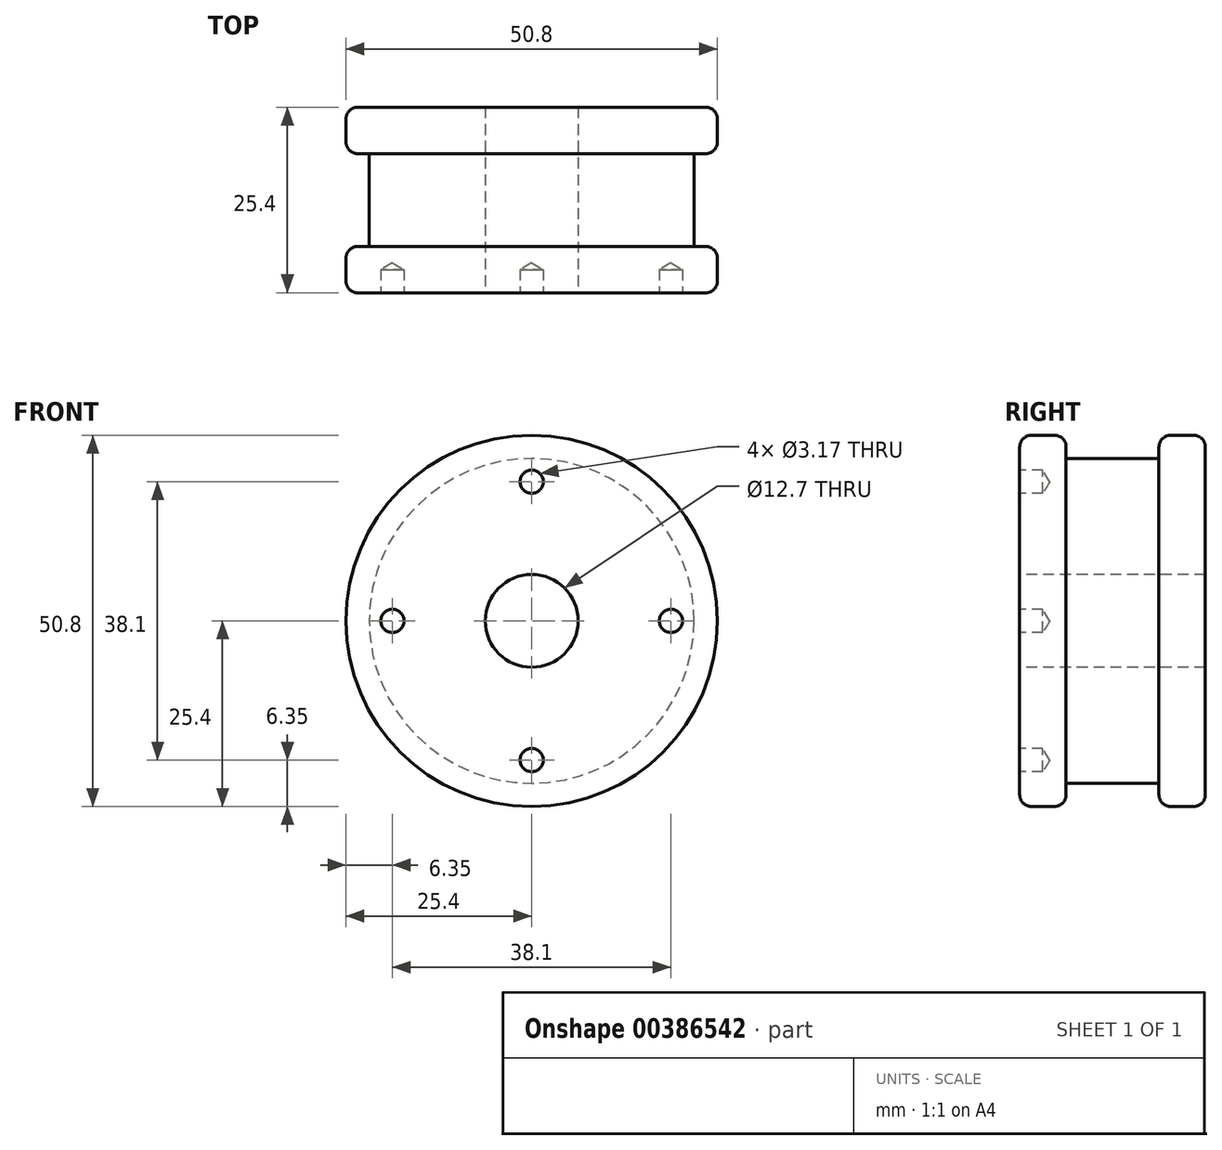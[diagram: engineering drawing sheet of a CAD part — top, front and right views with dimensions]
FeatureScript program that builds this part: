
annotation { "Feature Type Name" : "Feature", "Feature Type Description" : "" }
export const myFeature = defineFeature(function(context is Context, id is Id, definition is map)
    precondition{}
    {
        {
            var Q0;
            Q0=qCreatedBy(makeId("Front.planeOp"),FACE);
            var sketch = newSketch(context, id + "F0", { "sketchPlane" : qUnion([Q0])});
            skCircle(sketch, "E0", {"center": v(0, 0) * mm, "radius": 25.4 * mm});
            skSolve(sketch);
        }
        {
            var Q0;
            Q0 = qSketchRegion(id + "F0", true);
            extrude(context, id + "F1", {"entities" : qUnion([Q0]), "depth" : 6.35 * mm});
        }
        {
            var Q0;
            Q0=makeQuery(id+"F1.opExtrude","CAP_FACE",FACE,{"disambiguationData":[OSD([sQuery(id+"F0.wireOp",EDGE,"E0")])],"isStart":false});
            var sketch = newSketch(context, id + "F2", { "sketchPlane" : qUnion([Q0])});
            skCircle(sketch, "E1", {"center": v(0, 0) * mm, "radius": 22.23 * mm});
            skSolve(sketch);
        }
        {
            var Q0;
            Q0 = qSketchRegion(id + "F2", true);
            extrude(context, id + "F3", {"entities" : qUnion([Q0]), "operationType" : NewBodyOperationType.ADD, "depth" : 12.7 * mm});
        }
        {
            var Q0;
            Q0=makeQuery(id+"F3.opExtrude","CAP_FACE",FACE,{"disambiguationData":[OSD([sQuery(id+"F2.wireOp",EDGE,"E1")])],"isStart":false});
            var sketch = newSketch(context, id + "F4", { "sketchPlane" : qUnion([Q0])});
            skCircle(sketch, "E2", {"center": v(0, 0) * mm, "radius": 25.4 * mm});
            skSolve(sketch);
        }
        {
            var Q0;
            Q0 = qSketchRegion(id + "F4", true);
            extrude(context, id + "F5", {"entities" : qUnion([Q0]), "operationType" : NewBodyOperationType.ADD, "depth" : 6.35 * mm});
        }
        {
            var Q0;
            Q0=makeQuery(id+"F1.opExtrude","CAP_EDGE",EDGE,{"disambiguationData":[OSD([sQuery(id+"F0.wireOp",EDGE,"E0")])],"isStart":true});
            var Q1;
            Q1=makeQuery(id+"F1.opExtrude","CAP_EDGE",EDGE,{"disambiguationData":[OSD([sQuery(id+"F0.wireOp",EDGE,"E0")])],"isStart":false});
            var Q2;
            Q2=makeQuery(id+"F5.opExtrude","CAP_EDGE",EDGE,{"disambiguationData":[OSD([sQuery(id+"F4.wireOp",EDGE,"E2")])],"isStart":false});
            var Q3;
            Q3=makeQuery(id+"F5.opExtrude","CAP_EDGE",EDGE,{"disambiguationData":[OSD([sQuery(id+"F4.wireOp",EDGE,"E2")])],"isStart":true});
            var Q4;
            Q4=makeQuery(id+"F3.opExtrude","CAP_EDGE",EDGE,{"disambiguationData":[OSD([sQuery(id+"F2.wireOp",EDGE,"E1")])],"isStart":false});
            var Q5;
            Q5=makeQuery(id+"F3.opExtrude","CAP_EDGE",EDGE,{"disambiguationData":[OSD([sQuery(id+"F2.wireOp",EDGE,"E1")])],"isStart":true});
            fillet(context, id + "F6", {"entities" : qUnion([Q0, Q1, Q2, Q3, Q4, Q5]), "radius" : 1.59 * mm, "tangentPropagation" : true, "allowEdgeOverflow" : false});
        }
        {
            var Q0;
            Q0=makeQuery(id+"F5.opExtrude","CAP_FACE",FACE,{"disambiguationData":[OSD([sQuery(id+"F4.wireOp",EDGE,"E2")])],"isStart":false});
            var sketch = newSketch(context, id + "F7", { "sketchPlane" : qUnion([Q0])});
            skPoint(sketch, "E3", {"position": v(0, -19.05) * mm});
            skPoint(sketch, "E4", {"position": v(0, 19.05) * mm});
            skPoint(sketch, "E5", {"position": v(19.05, 0) * mm});
            skPoint(sketch, "E6", {"position": v(-19.05, 0) * mm});
            skPoint(sketch, "E7", {"position": v(0, 0) * mm});
            skSolve(sketch);
        }
        {
            var Q0;
            Q0=sQuery(id+"F7.wireOp",VERTEX,"E4");
            var Q1;
            Q1=sQuery(id+"F7.wireOp",VERTEX,"E5");
            var Q2;
            Q2=sQuery(id+"F7.wireOp",VERTEX,"E3");
            var Q3;
            Q3=sQuery(id+"F7.wireOp",VERTEX,"E6");
            var Q4;
            Q4=makeQuery(id+"F1.opExtrude","SWEPT_BODY",BODY,{"disambiguationData":[OSD([sQuery(id+"F0.wireOp",EDGE,"E0")])]});
            hole(context, id + "F8", {"style" : HoleStyle.SIMPLE, "endStyle" : HoleEndStyle.BLIND, "holeDiameter" : 3.17 * mm, "holeDepth" : 3.17 * mm, "isTappedThrough" : true, "tappedDepth" : 12.7 * mm, "tapClearance" : 3, "startFromSketch" : true, "locations" : qUnion([Q0, Q1, Q2, Q3]), "scope" : qUnion([Q4])});
        }
        {
            var Q0;
            Q0=sQuery(id+"F7.wireOp",VERTEX,"E7");
            var Q1;
            Q1=makeQuery(id+"F1.opExtrude","SWEPT_BODY",BODY,{"disambiguationData":[OSD([sQuery(id+"F0.wireOp",EDGE,"E0")])]});
            hole(context, id + "F9", {"style" : HoleStyle.SIMPLE, "endStyle" : HoleEndStyle.THROUGH, "holeDiameter" : 12.7 * mm, "isTappedThrough" : true, "tappedDepth" : 12.7 * mm, "tapClearance" : 3, "startFromSketch" : true, "locations" : qUnion([Q0]), "scope" : qUnion([Q1])});
        }
    });
